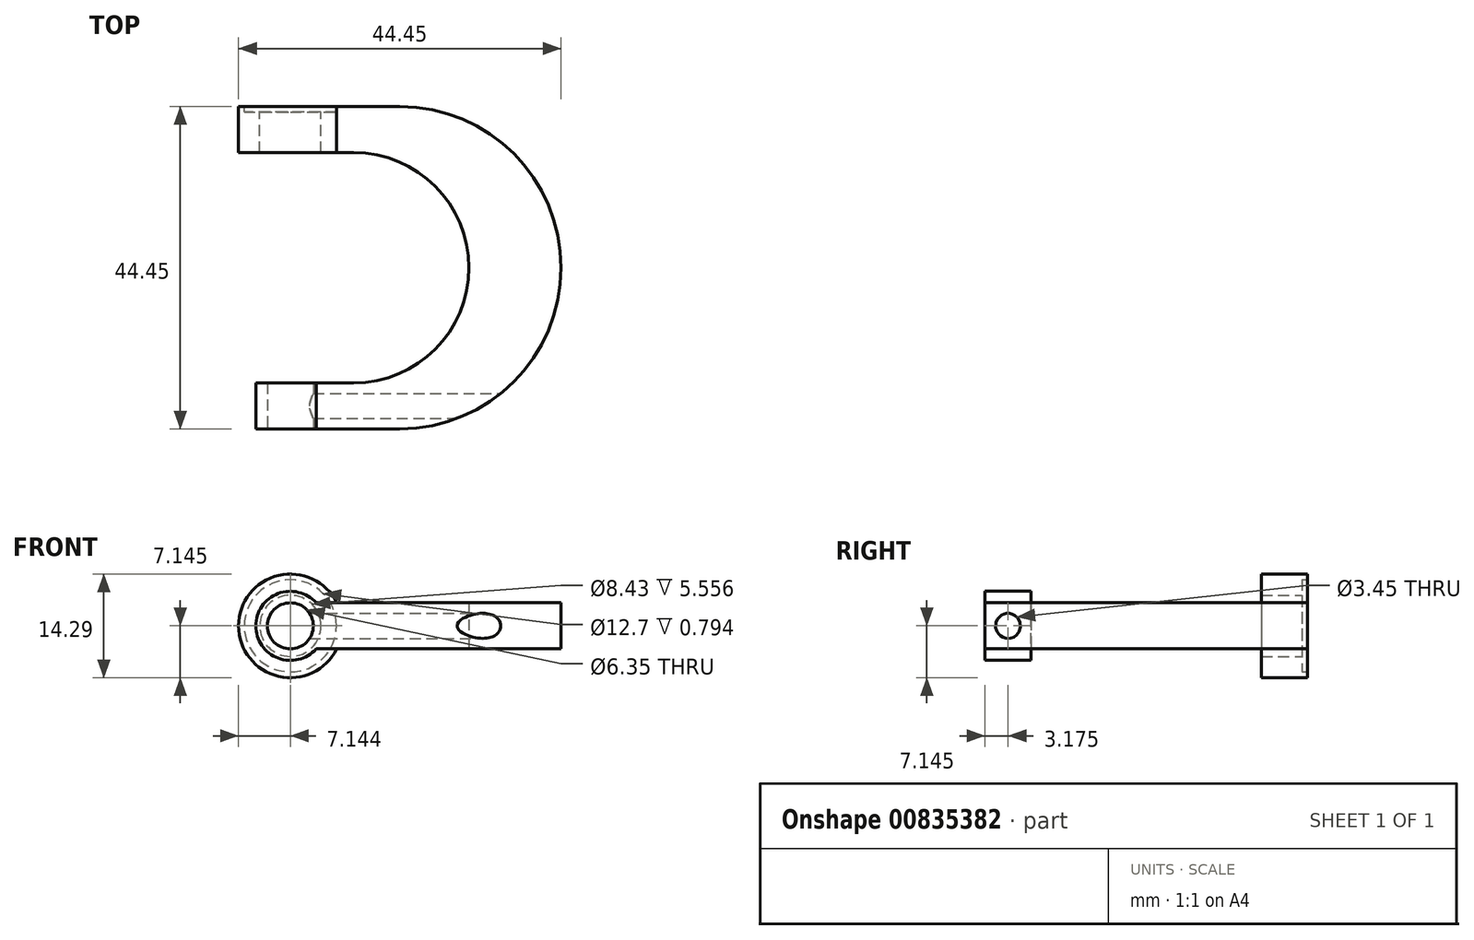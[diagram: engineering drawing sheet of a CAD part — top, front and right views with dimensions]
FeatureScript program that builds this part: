
annotation { "Feature Type Name" : "Feature", "Feature Type Description" : "" }
export const myFeature = defineFeature(function(context is Context, id is Id, definition is map)
    precondition{}
    {
        {
            var Q0;
            Q0=qCreatedBy(makeId("Front.planeOp"),FACE);
            var sketch = newSketch(context, id + "F0", { "sketchPlane" : qUnion([Q0])});
            skLineSegment(sketch, "E0.bottom", {"start": v(0, 0) * mm, "end": v(-44.45, 0) * mm});
            skLineSegment(sketch, "E0.top", {"start": v(0, 6.35) * mm, "end": v(-44.45, 6.35) * mm});
            skLineSegment(sketch, "E0.left", {"start": v(0, 0) * mm, "end": v(0, 6.35) * mm});
            skLineSegment(sketch, "E0.right", {"start": v(-44.45, 0) * mm, "end": v(-44.45, 6.35) * mm});
            skPoint(sketch, "E1.centerSnap0", {"position": v(-44.45, 3.17) * mm});
            skCircle(sketch, "E2", {"center": v(-37.3, 3.17) * mm, "radius": 7.14 * mm});
            skSolve(sketch);
        }
        {
            var Q0;
            {var subQ0=sQuery(id+"F0.wireOp",EDGE,"E0.left");Q0=makeQuery(id+"F0.imprint","IMPRINT",FACE,{"disambiguationData":[TD([[makeQuery(id+"F0.imprint","IMPRINT",EDGE,{"derivedFrom":subQ0}),1.0]])]});}
            var Q1;
            {var subQ0=sQuery(id+"F0.wireOp",EDGE,"E1");var subQ1=sQuery(id+"F0.wireOp",EDGE,"E0.bottom");var subQ2=makeQuery(id+"F0.imprint","INTERSECT",VERTEX,{"disambiguationData":[OD(0.0)],"derivedFrom":[subQ1,subQ0]});Q1=makeQuery(id+"F0.imprint","IMPRINT",FACE,{"disambiguationData":[TD([[makeQuery(id+"F0.imprint","IMPRINT",EDGE,{"disambiguationData":[TD([[subQ2,-1.0]])],"derivedFrom":subQ1}),-1.0]])]});}
            var Q2;
            {var subQ0=sQuery(id+"F0.wireOp",EDGE,"E1");var subQ1=sQuery(id+"F0.wireOp",EDGE,"E0.bottom");var subQ2=makeQuery(id+"F0.imprint","INTERSECT",VERTEX,{"disambiguationData":[OD(0.0)],"derivedFrom":[subQ1,subQ0]});Q2=makeQuery(id+"F0.imprint","IMPRINT",FACE,{"disambiguationData":[TD([[makeQuery(id+"F0.imprint","IMPRINT",EDGE,{"disambiguationData":[TD([[subQ2,-1.0]])],"derivedFrom":subQ1}),1.0]])]});}
            var Q3;
            {var subQ0=sQuery(id+"F0.wireOp",EDGE,"E1");var subQ1=sQuery(id+"F0.wireOp",EDGE,"E0.top");var subQ2=makeQuery(id+"F0.imprint","INTERSECT",VERTEX,{"disambiguationData":[OD(0.0)],"derivedFrom":[subQ1,subQ0]});Q3=makeQuery(id+"F0.imprint","IMPRINT",FACE,{"disambiguationData":[TD([[makeQuery(id+"F0.imprint","IMPRINT",EDGE,{"disambiguationData":[TD([[subQ2,-1.0]])],"derivedFrom":subQ1}),-1.0]])]});}
            extrude(context, id + "F1", {"entities" : qUnion([Q0, Q1, Q2, Q3]), "depth" : 44.45 * mm, "offsetDistance" : 25.4 * mm});
        }
        {
            var Q0;
            Q0=makeQuery(id+"F1.opExtrude","SWEPT_FACE",FACE,{"disambiguationData":[OSD([sQuery(id+"F0.wireOp",EDGE,"E0.top")])]});
            var sketch = newSketch(context, id + "F2", { "sketchPlane" : qUnion([Q0])});
            skLineSegment(sketch, "E3", {"start": v(-44.45, 0) * mm, "end": v(-22.23, 0) * mm});
            skLineSegment(sketch, "E4", {"start": v(-22.23, -44.45) * mm, "end": v(-44.45, -44.45) * mm});
            skLineSegment(sketch, "E5", {"start": v(-44.45, -44.45) * mm, "end": v(-44.45, -38.1) * mm});
            skLineSegment(sketch, "E6", {"start": v(-44.45, -38.1) * mm, "end": v(-28.57, -38.1) * mm});
            skLineSegment(sketch, "E7", {"start": v(-28.58, -6.35) * mm, "end": v(-44.45, -6.35) * mm});
            skLineSegment(sketch, "E8", {"start": v(-44.45, -6.35) * mm, "end": v(-44.45, 0) * mm});
            skArc(sketch, "E9", {"start": v(-28.57, -38.1) * mm, "mid": v(-12.7, -22.22) * mm, "end": v(-28.57, -6.35) * mm});
            skArc(sketch, "E10", {"start": v(-22.23, -44.45) * mm, "mid": v(0, -22.22) * mm, "end": v(-22.23, 0) * mm});
            skSolve(sketch);
        }
        {
            var Q0;
            Q0 = qSketchRegion(id + "F2", true);
            extrude(context, id + "F3", {"entities" : qUnion([Q0]), "operationType" : NewBodyOperationType.INTERSECT, "endBound" : BoundingType.SYMMETRIC, "depth" : 25.4 * mm, "offsetDistance" : 25.4 * mm});
        }
        {
            var Q0;
            Q0=makeQuery(id+"F1.opExtrude","CAP_FACE",FACE,{"disambiguationData":[OSD([sQuery(id+"F0.wireOp",EDGE,"E0.bottom"),sQuery(id+"F0.wireOp",EDGE,"E0.top"),sQuery(id+"F0.wireOp",EDGE,"E0.left"),sQuery(id+"F0.wireOp",EDGE,"E0.right"),sQuery(id+"F0.wireOp",EDGE,"1qjstD53-BZU3-N6s7-4aq1-33XG4RFPlDfV"),sQuery(id+"F0.wireOp",EDGE,"wEHJj6fN-Jbp2-WKGD-R3Ui-Z3DyBZedKB5S"),sQuery(id+"F0.wireOp",EDGE,"dDnwIX1L-gGQO-gSI1-RGQh-JWqJw8tpQSpo"),sQuery(id+"F0.wireOp",EDGE,"3mQwOFtE-9oil-iNGl-AxFZ-M0mTUi2Ror7S"),sQuery(id+"F0.wireOp",EDGE,"5a96FFVS-bLgL-ASgo-Oskf-x4BcF2Z54uqC"),sQuery(id+"F0.wireOp",EDGE,"FojXUcAo-j2Ns-me5k-ljT6-Bpl3sC6Bpak4")])],"isStart":true});
            var sketch = newSketch(context, id + "F4", { "sketchPlane" : qUnion([Q0])});
            skPoint(sketch, "E11", {"position": v(37.3, 3.17) * mm});
            skSolve(sketch);
        }
        {
            var Q0;
            Q0=sQuery(id+"F4.wireOp",VERTEX,"0fce52ad-bf62-477a-8368-785ab6c7edd4");
            var Q1;
            Q1=sQuery(id+"F4.wireOp",VERTEX,"E11");
            var Q2;
            Q2=makeQuery(id+"F1.opExtrude","SWEPT_BODY",BODY,{"disambiguationData":[OSD([sQuery(id+"F0.wireOp",EDGE,"E0.bottom"),sQuery(id+"F0.wireOp",EDGE,"E0.top"),sQuery(id+"F0.wireOp",EDGE,"E0.left"),sQuery(id+"F0.wireOp",EDGE,"E0.right"),sQuery(id+"F0.wireOp",EDGE,"1qjstD53-BZU3-N6s7-4aq1-33XG4RFPlDfV"),sQuery(id+"F0.wireOp",EDGE,"wEHJj6fN-Jbp2-WKGD-R3Ui-Z3DyBZedKB5S"),sQuery(id+"F0.wireOp",EDGE,"dDnwIX1L-gGQO-gSI1-RGQh-JWqJw8tpQSpo"),sQuery(id+"F0.wireOp",EDGE,"3mQwOFtE-9oil-iNGl-AxFZ-M0mTUi2Ror7S"),sQuery(id+"F0.wireOp",EDGE,"5a96FFVS-bLgL-ASgo-Oskf-x4BcF2Z54uqC"),sQuery(id+"F0.wireOp",EDGE,"FojXUcAo-j2Ns-me5k-ljT6-Bpl3sC6Bpak4")])]});
            hole(context, id + "F5", {"style" : HoleStyle.C_BORE, "endStyle" : HoleEndStyle.BLIND, "holeDiameter" : 8.43 * mm, "cBoreDiameter" : 12.7 * mm, "cBoreDepth" : 0.8 * mm, "majorDiameter" : 6.35 * mm, "holeDepth" : 6.35 * mm, "isTappedThrough" : true, "tappedDepth" : 12.7 * mm, "tapClearance" : 3, "locations" : qUnion([Q0, Q1]), "scope" : qUnion([Q2])});
        }
        {
            var Q0;
            Q0=makeQuery(id+"F1.opExtrude","CAP_FACE",FACE,{"disambiguationData":[OSD([sQuery(id+"F0.wireOp",EDGE,"E0.bottom"),sQuery(id+"F0.wireOp",EDGE,"E0.top"),sQuery(id+"F0.wireOp",EDGE,"E0.left"),sQuery(id+"F0.wireOp",EDGE,"E2")])],"isStart":false});
            var sketch = newSketch(context, id + "F6", { "sketchPlane" : qUnion([Q0])});
            skCircle(sketch, "E12", {"center": v(-37.3, 3.17) * mm, "radius": 3.18 * mm});
            skCircle(sketch, "E13", {"center": v(-37.3, 3.17) * mm, "radius": 4.76 * mm});
            skCircle(sketch, "E14", {"center": v(-37.3, 3.17) * mm, "radius": 7.14 * mm});
            skLineSegment(sketch, "E15", {"start": v(-30.9, 0) * mm, "end": v(-33.76, 0) * mm});
            skLineSegment(sketch, "E16", {"start": v(-30.9, 6.35) * mm, "end": v(-33.76, 6.35) * mm});
            skSolve(sketch);
        }
        {
            var Q0;
            {var subQ0=sQuery(id+"F6.wireOp",EDGE,"E15");Q0=makeQuery(id+"F6.imprint","IMPRINT",FACE,{"disambiguationData":[TD([[makeQuery(id+"F6.imprint","IMPRINT",EDGE,{"derivedFrom":subQ0}),1.0]])]});}
            var Q1;
            Q1=makeQuery(id+"F6.imprint","IMPRINT",FACE,{"disambiguationData":[TD([[makeQuery(id+"F6.imprint","IMPRINT",EDGE,{"derivedFrom":sQuery(id+"F6.wireOp",EDGE,"E12")}),1.0]])]});
            extrude(context, id + "F7", {"entities" : qUnion([Q0, Q1]), "operationType" : NewBodyOperationType.REMOVE, "oppositeDirection" : true, "depth" : 25.4 * mm, "offsetDistance" : 25.4 * mm});
        }
        {
            var Q0;
            Q0=qCreatedBy(makeId("Right.planeOp"),FACE);
            var sketch = newSketch(context, id + "F8", { "sketchPlane" : qUnion([Q0])});
            skCircle(sketch, "E17", {"center": v(-41.28, 3.18) * mm, "radius": 1.73 * mm});
            skSolve(sketch);
        }
        {
            var Q0;
            Q0=makeQuery(id+"F8.imprint","IMPRINT",FACE,{"disambiguationData":[TD([[makeQuery(id+"F8.imprint","IMPRINT",EDGE,{"derivedFrom":sQuery(id+"F8.wireOp",EDGE,"E17")}),1.0]])]});
            extrude(context, id + "F9", {"entities" : qUnion([Q0]), "operationType" : NewBodyOperationType.REMOVE, "oppositeDirection" : true, "depth" : 38.1 * mm, "offsetDistance" : 25.4 * mm});
        }
    });
